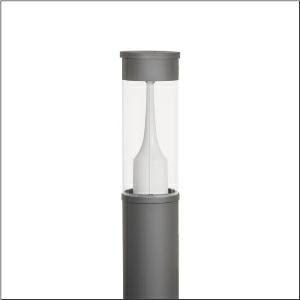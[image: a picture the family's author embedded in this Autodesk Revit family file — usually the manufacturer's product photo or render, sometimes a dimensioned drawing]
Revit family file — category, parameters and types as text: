
# Revit family: city-light_260_iq___st1_2a_5xa5295af14h_a960
name_source: partatom
category: Lighting Fixtures
units: mm (PartAtom-declared; Revit-internal decimal feet)

## family parameters
Cut with Voids When Loaded = No
Host = Face
Light Source = No
Part Type = Normal
Room Calculation Point = No
Round Connector Dimension = Use Diameter
Shared = No

## types (1)
- --- (1 x LED, 1540 lm, 12.9 W, 2200K)
    Apparent Load = 13 VA
    CIE Flux Codes = 22 61 93 96 100
    Color Rendering = 70
    Color Temperature = 2200K
    Default Elevation = 1800 mm
    Description = City-Light 260 iQ, light pillar, Module 540 iQ-SR, primary light control with 3 zone facetted reflector, of plastic, silver coated, highly specular, structured, primary optical cover: cover, of PMMA, transparent, partly coated, light distribution: ST1.2a, primary light characteristic: asymmetric, LED, High Power LED, rated luminous flux: 1.540lm, luminous efficacy: 119lm/W, light colour: 722, colour temperature: 2200K, control gear: ECG iQ, control: presetting dimming logarithmic, Street-Remote, Auto-Match, Temp-Guard, Lumen-Switch, Night-Set, Smart-Wire, Light-Fading, Desk-Remote (wireless, voltage-free reading and setting of iQ features in the workshop via application-optimized NFC function/RFID function), optimised constant luminous flux control (CLO 2.0), with terminal, 6-pole, max. 2.5mm², mains connection: 230..240V, AC, 50/60Hz, start of lifetime: 13W, end of service life: 13W, reduction: 6W, luminaire housing, cylindrical, of extruded aluminium section, coated, Siteco® metallic grey (DB 702S), length: 2.600mm, diameter: 200mm, Module 540 iQ-SR, traffic white (RAL 9016), equipment: standard, protection rating (complete): IP65, insulation class (complete): insulation class II (safety insulation), certification: CE, ENEC, VDE, packaging unit: 1 piece

Light Distribution: ST1.2a
    Height = 500 mm
    Lamp = 1 x LED
    Lamp Light Flux = 1540 lm
    Lamp Power = 12.9 W
    Lamp count = 1
    Length = 200 mm  [stored 0.656168 ft]
    Luminous efficacy = 119 lm/W
    Manufacturer = Siteco
    ModVariant = No
    Model = 5XA5295AF14H
    Mounting Place = Floor
    Mounting Type = Freestanding
    Number of Poles = 1
    OnlyDefault = Yes
    Power Factor = 1
    Product Name = City-Light 260 iQ | ST1.2a
    Product group = light pillar
    ProductGroupID = 1303
    Protection Class = Protection class II
    Protection Degree = IP 65
    RLX_Detail_Level = 1
    RLX_Emergency_Light_Flux = 0 lm
    RLX_Emergency_Type = 0
    RLX_Emergency_Type_DB = No
    RlxData = <blob elided: 60989 chars, md5=03f46790>
    Socket = socket
    Standby Power = 0 W
    System Light Flux = 1540 lm
    System Power = 13 W
    Type Comments = factory setting: luminous flux: 100 % | dim-lin: 254 | 516 mA
    Type Image = l_1006918.jpg
    URL = http://relux.com
    VarID = @adj_091559
    Voltage = 0 V
    Weight = 0.00 kg
    Width = 0 mm  [stored 0 ft]

note: [stored X ft] marks values corroborated as IEEE doubles in the binary element streams (Revit-internal decimal feet)

## geometry (parser evidence)
native form markers: Blend x4, Sweep x12
no freeform markers — native parametric forms only
